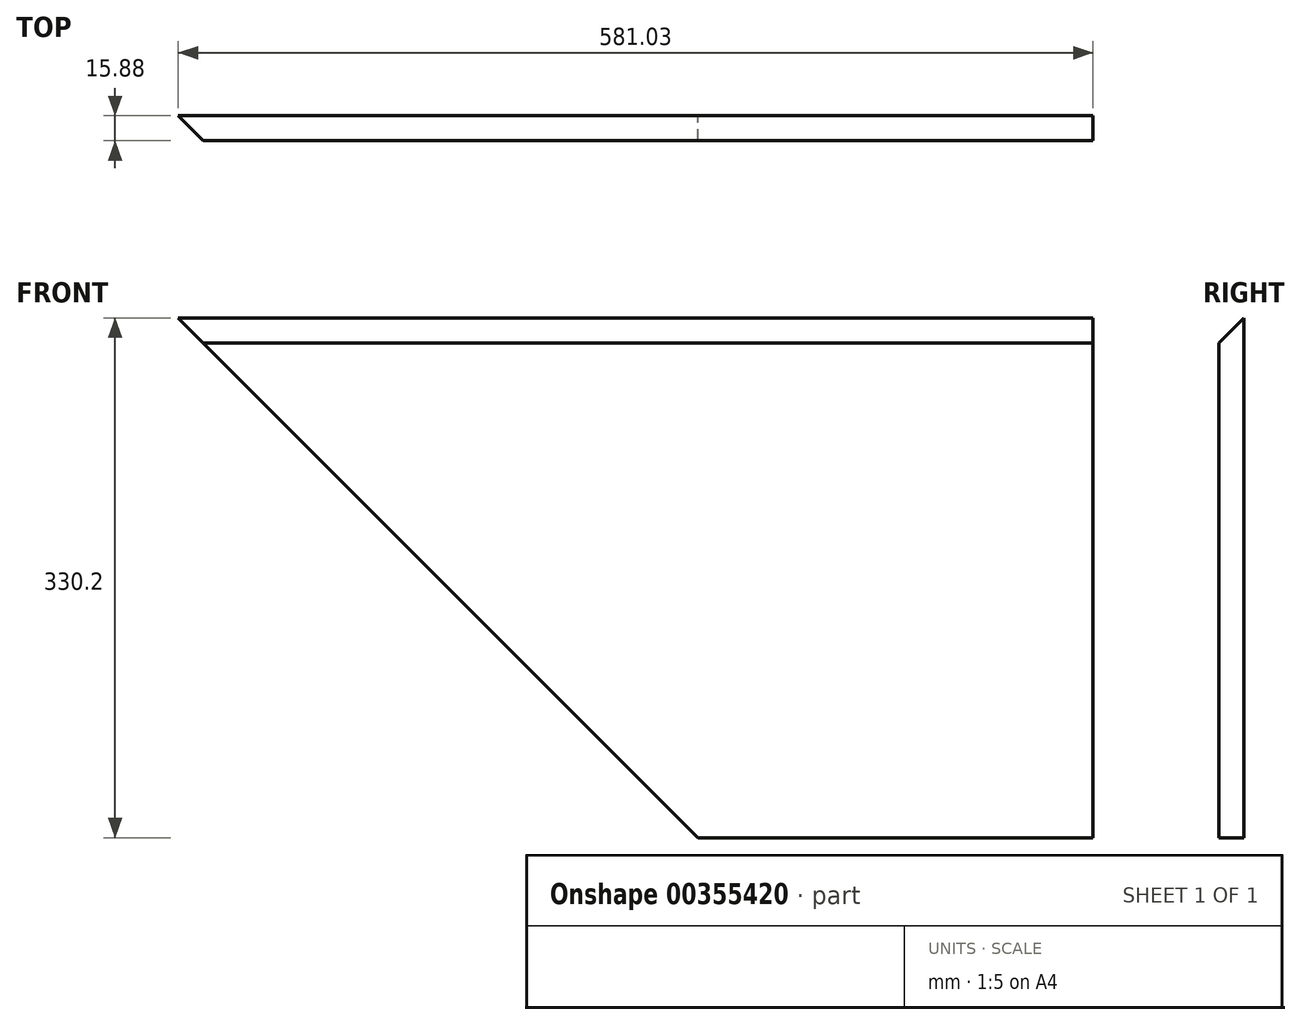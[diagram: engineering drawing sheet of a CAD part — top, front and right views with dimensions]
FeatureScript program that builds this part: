
annotation { "Feature Type Name" : "Feature", "Feature Type Description" : "" }
export const myFeature = defineFeature(function(context is Context, id is Id, definition is map)
    precondition{}
    {
        {
            var Q0;
            Q0=qCreatedBy(makeId("Front.planeOp"),FACE);
            var sketch = newSketch(context, id + "F0", { "sketchPlane" : qUnion([Q0])});
            skLineSegment(sketch, "E0.left", {"start": v(0, 0) * mm, "end": v(0, 330.2) * mm});
            skLineSegment(sketch, "E1", {"start": v(-250.83, 0) * mm, "end": v(0, 0) * mm});
            skLineSegment(sketch, "E2", {"start": v(-581.02, 330.2) * mm, "end": v(0, 330.2) * mm});
            skLineSegment(sketch, "E3", {"start": v(-581.02, 330.2) * mm, "end": v(-250.83, 0) * mm});
            skSolve(sketch);
        }
        {
            var Q0;
            Q0=makeQuery(id+"F0.imprint","IMPRINT",FACE,{"disambiguationData":[TD([[makeQuery(id+"F0.imprint","IMPRINT",EDGE,{"derivedFrom":sQuery(id+"F0.wireOp",EDGE,"E0.left")}),1.0]])]});
            extrude(context, id + "F1", {"entities" : qUnion([Q0]), "depth" : 15.88 * mm});
        }
        {
            var Q0;
            Q0=makeQuery(id+"F1.opExtrude","CAP_EDGE",EDGE,{"disambiguationData":[OSD([sQuery(id+"F0.wireOp",EDGE,"E2")])],"isStart":false});
            chamfer(context, id + "F2", {"entities" : qUnion([Q0]), "width" : 15.88 * mm, "tangentPropagation" : true});
        }
    });
